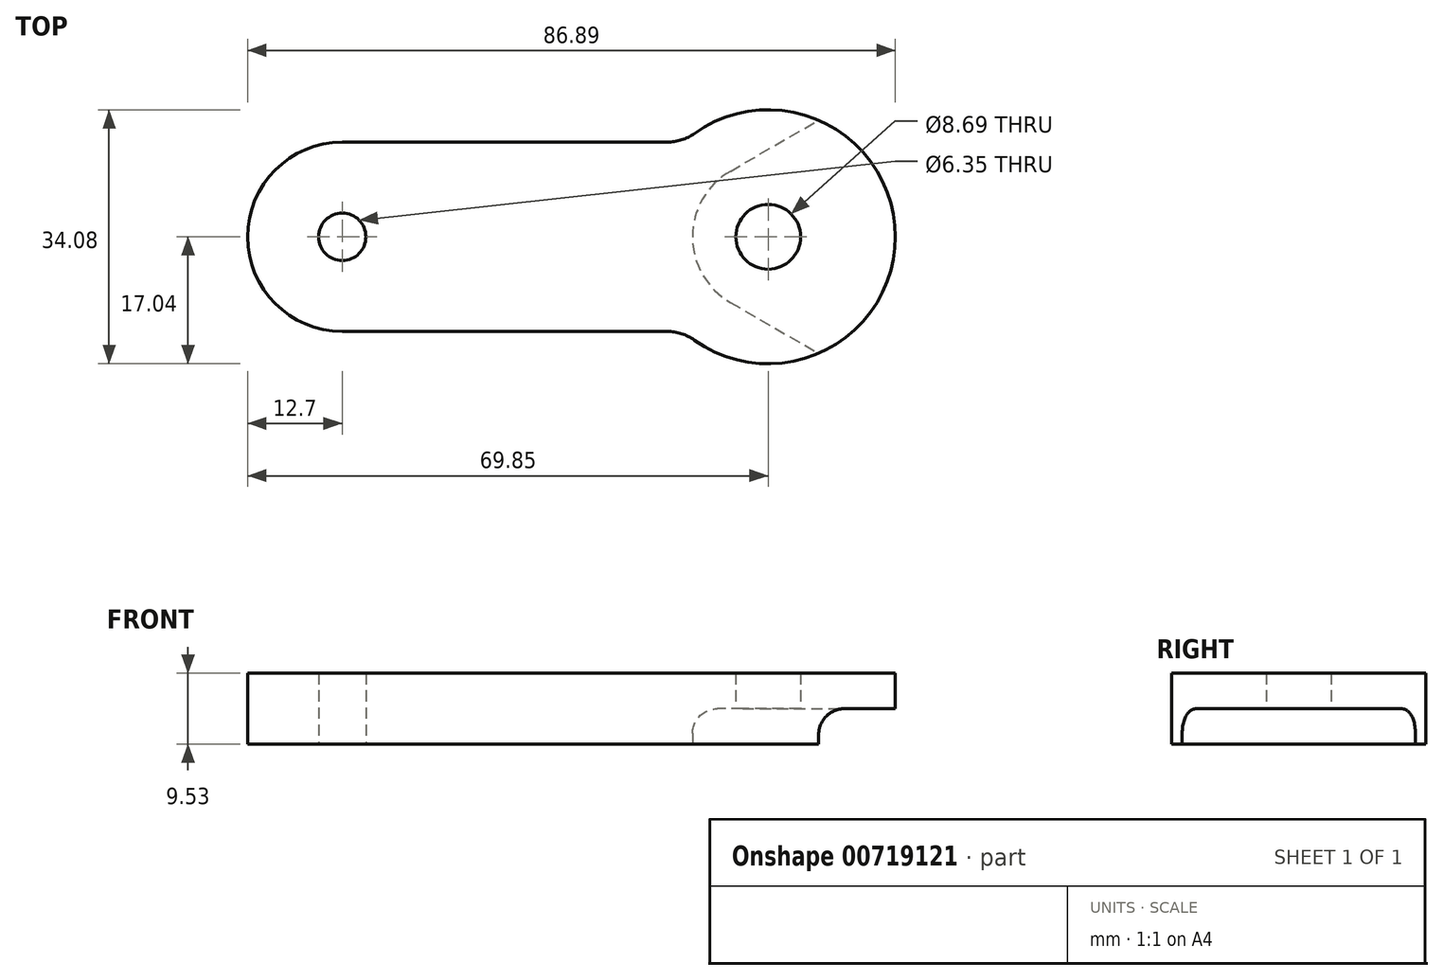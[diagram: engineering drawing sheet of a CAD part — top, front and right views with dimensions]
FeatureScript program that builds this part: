
annotation { "Feature Type Name" : "Feature", "Feature Type Description" : "" }
export const myFeature = defineFeature(function(context is Context, id is Id, definition is map)
    precondition{}
    {
        {
            var Q0;
            Q0=qCreatedBy(makeId("Top.planeOp"),FACE);
            var sketch = newSketch(context, id + "F0", { "sketchPlane" : qUnion([Q0])});
            skCircle(sketch, "E0", {"center": v(0, 0) * mm, "radius": 4.34 * mm});
            skArc(sketch, "E1", {"start": v(-9.9, -13.88) * mm, "mid": v(17.04, 0) * mm, "end": v(-9.9, 13.88) * mm});
            skCircle(sketch, "E2", {"center": v(-57.15, 0) * mm, "radius": 3.18 * mm});
            skArc(sketch, "E3", {"start": v(-57.15, 12.7) * mm, "mid": v(-69.85, 0) * mm, "end": v(-57.15, -12.7) * mm});
            skLineSegment(sketch, "E4", {"start": v(-57.15, 12.7) * mm, "end": v(-13.58, 12.7) * mm});
            skLineSegment(sketch, "E5", {"start": v(-57.15, 0) * mm, "end": v(0, 0) * mm, "construction": true});
            skLineSegment(sketch, "E6.MirrorCS", {"start": v(-57.15, -12.7) * mm, "end": v(-13.58, -12.7) * mm});
            skPoint(sketch, "E7.visualSharp", {"position": v(-11.37, 12.7) * mm});
            skArc(sketch, "E7.filletArc", {"start": v(-13.58, 12.7) * mm, "mid": v(-11.64, 13) * mm, "end": v(-9.9, 13.88) * mm});
            skPoint(sketch, "E8.visualSharp", {"position": v(-11.37, -12.7) * mm});
            skArc(sketch, "E8.filletArc", {"start": v(-9.9, -13.88) * mm, "mid": v(-11.64, -13) * mm, "end": v(-13.58, -12.7) * mm});
            skSolve(sketch);
        }
        {
            var Q0;
            Q0=makeQuery(id+"F0.imprint","IMPRINT",FACE,{"disambiguationData":[TD([[makeQuery(id+"F0.imprint","IMPRINT",EDGE,{"derivedFrom":sQuery(id+"F0.wireOp",EDGE,"E0")}),-1.0]])]});
            extrude(context, id + "F1", {"entities" : qUnion([Q0]), "depth" : 9.52 * mm, "offsetDistance" : 25.4 * mm});
        }
        {
            var Q0;
            Q0=makeQuery(id+"F1.opExtrude","CAP_FACE",FACE,{"disambiguationData":[OSD([sQuery(id+"F0.wireOp",EDGE,"E0"),sQuery(id+"F0.wireOp",EDGE,"E1"),sQuery(id+"F0.wireOp",EDGE,"E2"),sQuery(id+"F0.wireOp",EDGE,"E3"),sQuery(id+"F0.wireOp",EDGE,"E4"),sQuery(id+"F0.wireOp",EDGE,"E6.MirrorCS"),sQuery(id+"F0.wireOp",EDGE,"E7.filletArc"),sQuery(id+"F0.wireOp",EDGE,"E8.filletArc")])],"isStart":true});
            var sketch = newSketch(context, id + "F2", { "sketchPlane" : qUnion([Q0])});
            skArc(sketch, "E9", {"start": v(-5.08, 8.8) * mm, "mid": v(-8.8, 5.08) * mm, "end": v(-10.16, 0) * mm});
            skLineSegment(sketch, "E10", {"start": v(27.94, 0) * mm, "end": v(27.94, 27.86) * mm});
            skLineSegment(sketch, "E11", {"start": v(-5.08, 8.8) * mm, "end": v(27.94, 27.86) * mm});
            skLineSegment(sketch, "E12", {"start": v(-10.16, 0) * mm, "end": v(27.94, 0) * mm, "construction": true});
            skArc(sketch, "E13.MirrorCS", {"start": v(-5.08, -8.8) * mm, "mid": v(-8.8, -5.08) * mm, "end": v(-10.16, 0) * mm});
            skLineSegment(sketch, "E14.MirrorCS", {"start": v(-5.08, -8.8) * mm, "end": v(27.94, -27.86) * mm});
            skLineSegment(sketch, "E15.MirrorCS", {"start": v(27.94, 0) * mm, "end": v(27.94, -27.86) * mm});
            skSolve(sketch);
        }
        {
            var Q0;
            {var subQ2=sQuery(id+"F2.wireOp",EDGE,"E9");Q0=makeQuery(id+"F2.imprint","IMPRINT",FACE,{"disambiguationData":[TD([[makeQuery(id+"F2.imprint","IMPRINT",EDGE,{"derivedFrom":subQ2}),1.0]])]});}
            extrude(context, id + "F3", {"entities" : qUnion([Q0]), "operationType" : NewBodyOperationType.REMOVE, "oppositeDirection" : true, "depth" : 4.75 * mm, "offsetDistance" : 25.4 * mm});
        }
        {
            var Q0;
            Q0=makeQuery(id+"F3.boolean.opBoolean","COPY",EDGE,{"derivedFrom":makeQuery(id+"F3.opExtrude","CAP_EDGE",EDGE,{"disambiguationData":[OSD([sQuery(id+"F2.wireOp",EDGE,"E11")])],"isStart":false})});
            fillet(context, id + "F4", {"entities" : qUnion([Q0]), "radius" : 3.3 * mm, "tangentPropagation" : true, "allowEdgeOverflow" : false});
        }
    });
